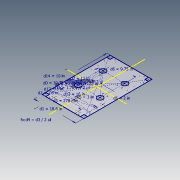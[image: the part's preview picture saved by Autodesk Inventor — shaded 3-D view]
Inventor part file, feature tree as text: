
AUTODESK INVENTOR PART (.ipt)
format: ipt  version: 2020.3 (Build 243373000, 373)  size: 275,456 bytes
history: native  units: in
note: dims shown in document units (in); Inventor stores cm internally (conversion verified against a paired STEP export)
features: hole x3, sketch x2, extrude x2, pattern_linear x2, mirror x1, fillet x1
ambient origin geometry x8: Origin, YZ Plane, XZ Plane, XY Plane, X Axis, Y Axis, Z Axis, Center Point
bodies: Solid1 (feature_tree)
feature tree (11):
  sketch  "Sketch1"  dims[d0=30.25in d1=18.6in]
  extrude  "Extrusion1"  Depth=18.6in
  hole  "Hole1"  [1 undecoded]
  mirror  "Mirror1"
  hole  "Hole2"  [1 undecoded]
  pattern_linear  "Rectangular Pattern1"  Spacing1=2.0in  [1 undecoded]
  hole  "Hole3"  [1 undecoded]
  extrude  "Extrusion2"  Depth=0.125in
  pattern_linear  "Rectangular Pattern2"  Spacing1=2.5in  [1 undecoded]
  fillet  "Fillet1"  Radius=3.25in
  sketch  "Sketch2"  dims[d2=1.6in d3=10.6299in d4=5.315in d5=2.0in d6=9.75in d7=11.0in d8=2.5in d9=3.25in d11=0.875in d12=3.0in d13=16.0in d14=10.0in d15=0.25in d16=0.0in d17=0.1276in d18=0.315in d19=0.119in d20=0.25in d21=0.5635in d22=0.465in d23=0.8108in d24=0.17in d25=0.75in d26=0.119in d27=0.25in d28=0.5635in d29=1.0in d30=0.8108in d31=0.7874in d33=11.0in d34=0.7874in d36=9.75in d37=29.0in d38=17.35in d39=6.5in d40=6.5in d41=12.0in d42=12.0in d43=0.266in d44=0.75in d45=0.438in d46=0.25in d47=0.5635in d48=1.0in d49=0.8108in d50=0.875in d51=0.125in d52=0.325in d53=0.125in d54=0.125in d55=2.25in d56=0.0in d57=0.0in d58=0.7874in d60=6.5in d61=0.7874in d63=9.75in d64=0.125in d65=3.0in]
note: 5 required parameter values undecoded (feature->parameter linkage not recoverable at this tier; creation-order binding heuristic only, values carry confidence <= 0.55)
